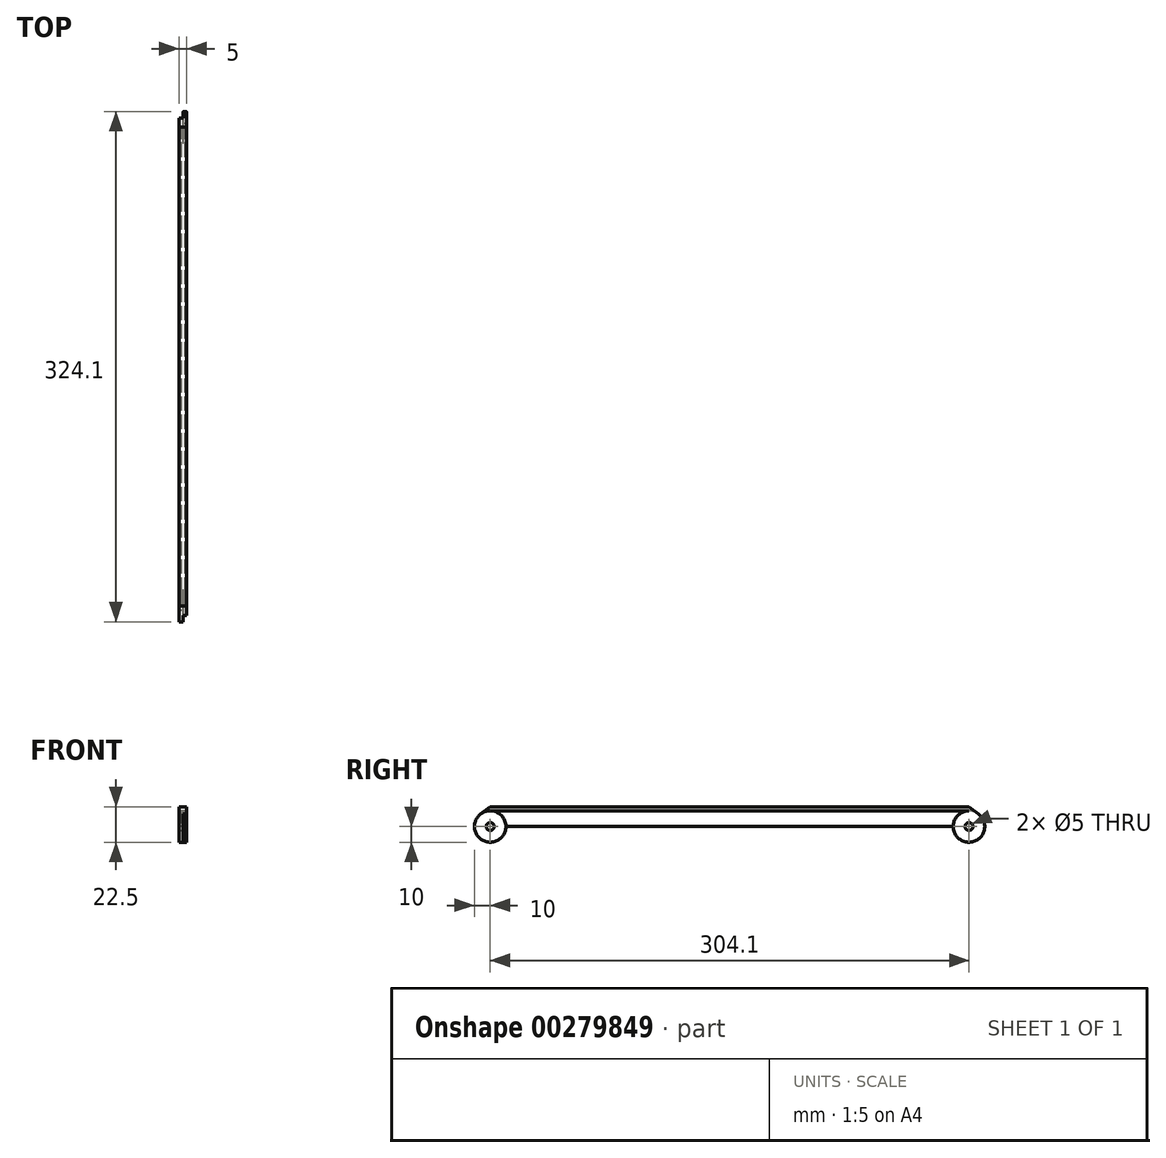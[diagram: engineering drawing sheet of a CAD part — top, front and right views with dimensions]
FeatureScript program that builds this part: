
annotation { "Feature Type Name" : "Feature", "Feature Type Description" : "" }
export const myFeature = defineFeature(function(context is Context, id is Id, definition is map)
    precondition{}
    {
        {
            var Q0;
            Q0=qCreatedBy(makeId("Right.planeOp"),FACE);
            var sketch = newSketch(context, id + "F0", { "sketchPlane" : qUnion([Q0])});
            skCircle(sketch, "E0", {"center": v(152.05, -12.5) * mm, "radius": 10 * mm});
            skCircle(sketch, "E1", {"center": v(-152.05, -12.5) * mm, "radius": 10 * mm});
            skCircle(sketch, "E2", {"center": v(152.05, -12.5) * mm, "radius": 2.5 * mm});
            skCircle(sketch, "E3", {"center": v(-152.05, -12.5) * mm, "radius": 2.5 * mm});
            skLineSegment(sketch, "E4", {"start": v(152.05, -2.5) * mm, "end": v(-152.05, -2.5) * mm});
            skLineSegment(sketch, "E5", {"start": v(152.05, 0) * mm, "end": v(-152.05, 0) * mm});
            skLineSegment(sketch, "E6", {"start": v(142.05, -12.5) * mm, "end": v(-142.05, -12.5) * mm});
            skLineSegment(sketch, "E7", {"start": v(152.05, 0) * mm, "end": v(158.05, -4.5) * mm});
            skLineSegment(sketch, "E8", {"start": v(-152.05, 0) * mm, "end": v(-158.05, -4.5) * mm});
            skLineSegment(sketch, "E9", {"start": v(152.05, -12.5) * mm, "end": v(142.05, -12.5) * mm, "construction": true});
            skLineSegment(sketch, "E10", {"start": v(-142.05, -12.5) * mm, "end": v(-152.05, -12.5) * mm, "construction": true});
            skLineSegment(sketch, "E11", {"start": v(152.05, -12.5) * mm, "end": v(152.05, -2.5) * mm, "construction": true});
            skLineSegment(sketch, "E12", {"start": v(-152.05, -12.5) * mm, "end": v(-152.05, -2.5) * mm, "construction": true});
            skLineSegment(sketch, "E13", {"start": v(152.05, -2.5) * mm, "end": v(152.05, 0) * mm, "construction": true});
            skLineSegment(sketch, "E14", {"start": v(-152.05, -2.5) * mm, "end": v(-152.05, 0) * mm, "construction": true});
            skSolve(sketch);
        }
        {
            var Q0;
            {var subQ0=sQuery(id+"F0.wireOp",EDGE,"E4");Q0=makeQuery(id+"F0.imprint","IMPRINT",FACE,{"disambiguationData":[TD([[makeQuery(id+"F0.imprint","IMPRINT",EDGE,{"derivedFrom":subQ0}),-1.0]])]});}
            extrude(context, id + "F1", {"entities" : qUnion([Q0]), "endBound" : BoundingType.SYMMETRIC, "depth" : 5 * mm});
        }
        {
            var Q0;
            Q0=makeQuery(id+"F0.imprint","IMPRINT",FACE,{"disambiguationData":[TD([[makeQuery(id+"F0.imprint","IMPRINT",EDGE,{"derivedFrom":sQuery(id+"F0.wireOp",EDGE,"E3")}),-1.0]])]});
            extrude(context, id + "F2", {"entities" : qUnion([Q0]), "operationType" : NewBodyOperationType.ADD, "oppositeDirection" : true, "depth" : 2.5 * mm});
        }
        {
            var Q0;
            Q0=makeQuery(id+"F0.imprint","IMPRINT",FACE,{"disambiguationData":[TD([[makeQuery(id+"F0.imprint","IMPRINT",EDGE,{"derivedFrom":sQuery(id+"F0.wireOp",EDGE,"E2")}),-1.0]])]});
            extrude(context, id + "F3", {"entities" : qUnion([Q0]), "operationType" : NewBodyOperationType.ADD, "depth" : 2.5 * mm});
        }
        {
            var Q0;
            {var subQ0=sQuery(id+"F0.wireOp",EDGE,"E4");Q0=makeQuery(id+"F0.imprint","IMPRINT",FACE,{"disambiguationData":[TD([[makeQuery(id+"F0.imprint","IMPRINT",EDGE,{"derivedFrom":subQ0}),1.0]])]});}
            extrude(context, id + "F4", {"entities" : qUnion([Q0]), "operationType" : NewBodyOperationType.ADD, "endBound" : BoundingType.SYMMETRIC, "depth" : 2.5 * mm});
        }
    });
